# Revit family: Sanitary_Showers_hansgrohe_15571AUS-ShowerSelect-Comfort-E-Thermost_new
name_source: partatom
category: Plumbing Fixtures
revit_build: Autodesk Revit 2018 (Build: 20170223_1515(x64)
units: mm (PartAtom-declared; Revit-internal decimal feet)

## family parameters
Always vertical = No
Cut with Voids When Loaded = No
OmniClass Number = 23.31.17.00
OmniClass Title = Showers
Part Type = Normal
Room Calculation Point = No
Round Connector Dimension = Use Diameter
Shared = No
Work Plane-Based = Yes

## types (5) — shared parameters
Always visible = Yes
BIMobject category = Showers
Default Elevation = 1219.2 mm  [stored 4 ft]
Description = ShowerSelect Comfort E Thermostat for concealed installation for 1 function
Design country = Germany
Edition number = 1
IFC Classification = Sanitary Terminal
Manufacturer = Hansgrohe
Manufacturer country = Germany
Manufacturer name = hansgrohe
Masterformat 2014 Code = 22 41 23
Masterformat 2014 Description = Residential Showers
Model = 15571AUS
OmniClass Code = 23-31 17 00
OmniClass Description = Showers
Product Guid = 963deb1e-fc7c-4599-a43b-fc39c2d2d8e1
Product SKU = 15571AUS
Product data url = https://bimobject.com
Product name = 15571AUS ShowerSelect Comfort E Thermostat for concealed installation for 1 function
Product url = https://www.hansgrohe.com
QR code = https://bimobject.com
UNSPSC Code = 30181503
URL = https://www.hansgrohe.com
Uniclass 2015 Code = Pr_40_20_87_76
Uniclass 2015 Name = Shower heads
Uniformat II Code = D2010
Uniformat II Description = Plumbing Fixtures
Weight Net (Kg) = 2.4

## per-type parameters (varying)
| type | Material 1 |
| 703 Matte White | Hansgrohe - Metal - 703 Matte White |
| 673 Matte Black | Hansgrohe - Metal - 673 Matte Black |
| 343 Brushed Black Chrome | Hansgrohe - Metal - 343 Brushed Black Chrome |
| 143 Brushed Bronze | Hansgrohe - Metal - 143 Brushed Bronze |
| 003 Chrome | Hansgrohe - Metal - 003 Chrome |

note: [stored X ft] marks values corroborated as IEEE doubles in the binary element streams (Revit-internal decimal feet)

## geometry (parser evidence)
native form markers: Sweep x2
no freeform markers — native parametric forms only
